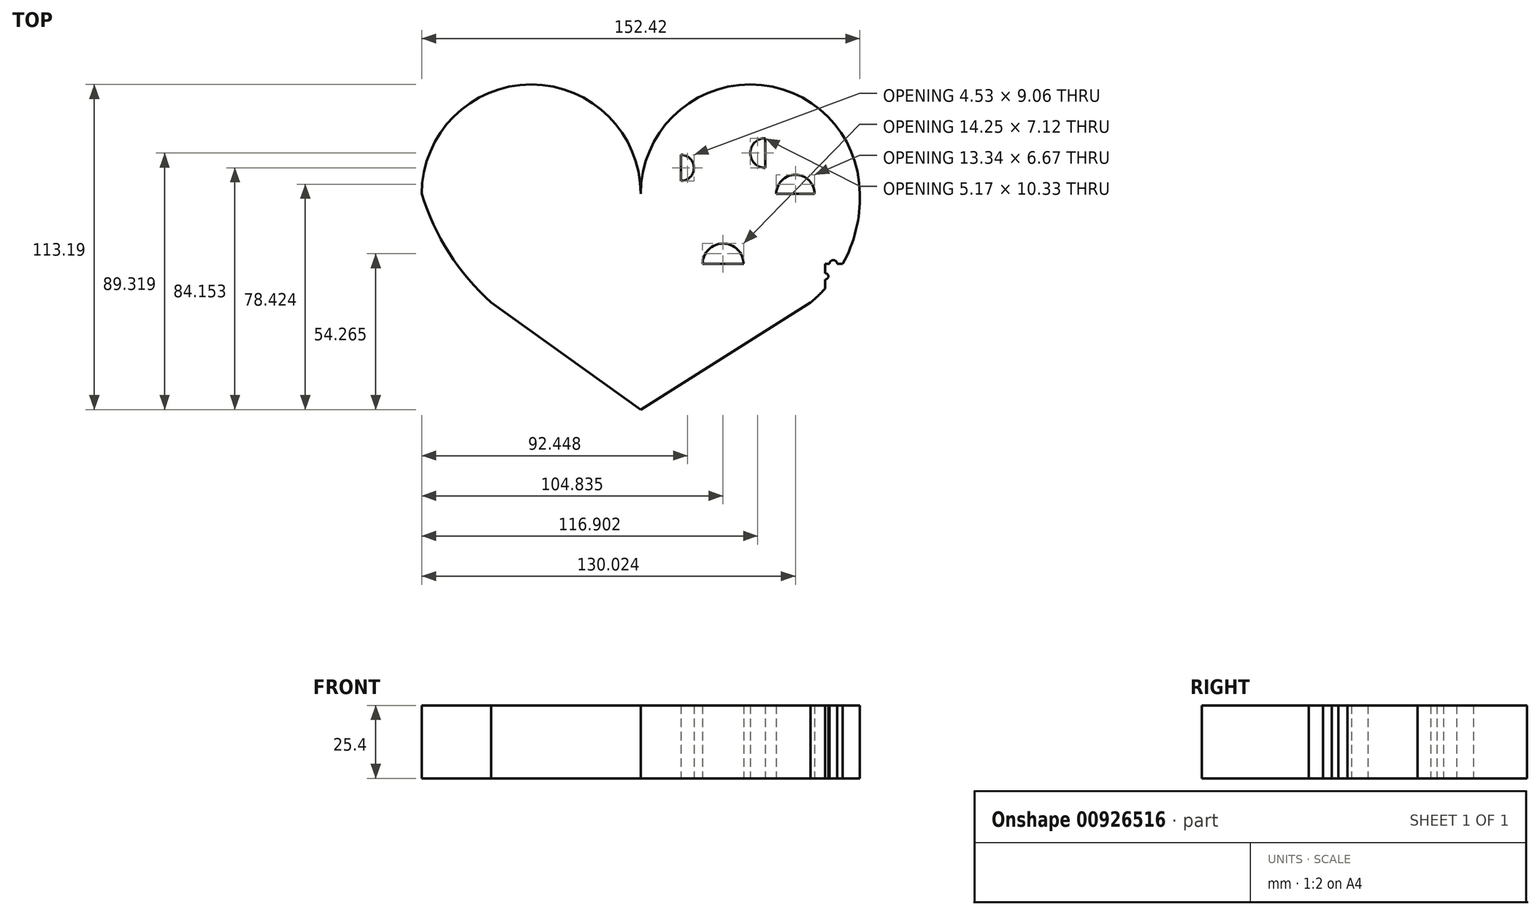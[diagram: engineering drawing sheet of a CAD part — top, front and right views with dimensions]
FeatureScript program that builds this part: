
annotation { "Feature Type Name" : "Feature", "Feature Type Description" : "" }
export const myFeature = defineFeature(function(context is Context, id is Id, definition is map)
    precondition{}
    {
        {
            var Q0;
            Q0=qCreatedBy(makeId("Top.planeOp"),FACE);
            var sketch = newSketch(context, id + "F0", { "sketchPlane" : qUnion([Q0])});
            skLineSegment(sketch, "E0", {"start": v(0, 0) * mm, "end": v(76.2, 0) * mm});
            skArc(sketch, "E1", {"start": v(76.2, 0) * mm, "mid": v(38.1, 38.1) * mm, "end": v(0, 0) * mm});
            skLineSegment(sketch, "E2", {"start": v(0, 0) * mm, "end": v(-76.2, 0) * mm});
            skArc(sketch, "E3", {"start": v(0, 0) * mm, "mid": v(-38.1, 38.1) * mm, "end": v(-76.2, 0) * mm});
            skArc(sketch, "E4", {"start": v(-76.2, 0) * mm, "mid": v(-66.69, -20.55) * mm, "end": v(-52.03, -37.8) * mm});
            skArc(sketch, "E5", {"start": v(59.1, -37.8) * mm, "mid": v(72.02, -20.88) * mm, "end": v(76.2, 0) * mm});
            skLineSegment(sketch, "E6", {"start": v(-52.03, -37.8) * mm, "end": v(0, -75.09) * mm});
            skLineSegment(sketch, "E7", {"start": v(0, -75.09) * mm, "end": v(59.1, -37.8) * mm});
            skLineSegment(sketch, "E8", {"start": v(-38.1, 38.1) * mm, "end": v(-38.1, -47.78) * mm});
            skLineSegment(sketch, "E9", {"start": v(-64.08, 27.87) * mm, "end": v(-64.08, -24.39) * mm});
            skLineSegment(sketch, "E10", {"start": v(-12.26, 28) * mm, "end": v(-12.26, -66.3) * mm});
            skLineSegment(sketch, "E11", {"start": v(13.98, 29.5) * mm, "end": v(13.98, -66.27) * mm});
            skLineSegment(sketch, "E12", {"start": v(64.16, 27.8) * mm, "end": v(64.16, -32.94) * mm});
            skLineSegment(sketch, "E13", {"start": v(-69.99, 20.85) * mm, "end": v(-6.21, 20.85) * mm});
            skLineSegment(sketch, "E14.bottom", {"start": v(6.21, 20.85) * mm, "end": v(69.99, 20.85) * mm});
            skLineSegment(sketch, "E14.top", {"start": v(6.21, 20.85) * mm, "end": v(69.99, 20.85) * mm});
            skLineSegment(sketch, "E14.left", {"start": v(6.21, 20.85) * mm, "end": v(6.21, 20.85) * mm});
            skLineSegment(sketch, "E14.right", {"start": v(69.99, 20.85) * mm, "end": v(69.99, 20.85) * mm});
            skLineSegment(sketch, "E15", {"start": v(-76.2, 0) * mm, "end": v(76.2, 0) * mm});
            skLineSegment(sketch, "E16", {"start": v(-64.08, -24.39) * mm, "end": v(70.25, -24.39) * mm});
            skLineSegment(sketch, "E17", {"start": v(-38.1, -47.78) * mm, "end": v(43.29, -47.78) * mm});
            skLineSegment(sketch, "E18", {"start": v(43.29, -47.78) * mm, "end": v(43.29, 37.75) * mm});
            skArc(sketch, "E19", {"start": v(-65.57, 20.85) * mm, "mid": v(-66.94, 22.19) * mm, "end": v(-68.32, 20.85) * mm});
            skArc(sketch, "E20", {"start": v(-64.08, 25.31) * mm, "mid": v(-65.33, 24.01) * mm, "end": v(-64.08, 22.71) * mm});
            skArc(sketch, "E21", {"start": v(-44.59, 20.85) * mm, "mid": v(-50, 25.72) * mm, "end": v(-55.4, 20.85) * mm});
            skArc(sketch, "E22", {"start": v(-38.1, 33.7) * mm, "mid": v(-43, 29.5) * mm, "end": v(-38.1, 25.31) * mm});
            skArc(sketch, "E23", {"start": v(-32.25, 20.85) * mm, "mid": v(-24.93, 15.14) * mm, "end": v(-17.62, 20.85) * mm});
            skArc(sketch, "E24", {"start": v(-12.26, 25.31) * mm, "mid": v(-15.3, 24.01) * mm, "end": v(-12.26, 22.71) * mm});
            skArc(sketch, "E25", {"start": v(-10.69, 20.85) * mm, "mid": v(-9.65, 18.8) * mm, "end": v(-8.62, 20.85) * mm});
            skArc(sketch, "E26", {"start": v(-64.08, 14.25) * mm, "mid": v(-68.2, 9.75) * mm, "end": v(-64.08, 5.25) * mm});
            skArc(sketch, "E27", {"start": v(-72.46, 0) * mm, "mid": v(-69.6, -2.41) * mm, "end": v(-66.75, 0) * mm});
            skArc(sketch, "E28", {"start": v(-46.12, 0) * mm, "mid": v(-50.71, 4.13) * mm, "end": v(-55.3, 0) * mm});
            skArc(sketch, "E29", {"start": v(-38.1, 4.4) * mm, "mid": v(-33.7, 9.23) * mm, "end": v(-38.1, 14.06) * mm});
            skArc(sketch, "E30", {"start": v(-64.08, -6.97) * mm, "mid": v(-67.6, -12.07) * mm, "end": v(-64.08, -17.17) * mm});
            skArc(sketch, "E31", {"start": v(-45.1, -24.39) * mm, "mid": v(-50.74, -16.9) * mm, "end": v(-56.38, -24.39) * mm});
            skArc(sketch, "E32", {"start": v(-38.1, -20) * mm, "mid": v(-32.5, -13.15) * mm, "end": v(-38.1, -6.3) * mm});
            skArc(sketch, "E33", {"start": v(-30.77, 0) * mm, "mid": v(-24.93, -6.3) * mm, "end": v(-19.1, 0) * mm});
            skArc(sketch, "E34", {"start": v(-12.26, 6.63) * mm, "mid": v(-6.96, 10.1) * mm, "end": v(-12.26, 13.57) * mm});
            skArc(sketch, "E35", {"start": v(-12.26, -17.17) * mm, "mid": v(-8.44, -13.07) * mm, "end": v(-12.26, -8.97) * mm});
            skArc(sketch, "E36", {"start": v(-38.1, -31) * mm, "mid": v(-43.58, -35.9) * mm, "end": v(-38.1, -40.81) * mm});
            skArc(sketch, "E37", {"start": v(-27.8, -24.39) * mm, "mid": v(-24.06, -29.29) * mm, "end": v(-20.3, -24.39) * mm});
            skArc(sketch, "E38", {"start": v(-18.77, -47.78) * mm, "mid": v(-24.34, -38.75) * mm, "end": v(-29.92, -47.78) * mm});
            skArc(sketch, "E39", {"start": v(-12.26, -41) * mm, "mid": v(-6.98, -36.58) * mm, "end": v(-12.26, -32.16) * mm});
            skArc(sketch, "E40", {"start": v(-12.26, -52.9) * mm, "mid": v(-16.92, -57.22) * mm, "end": v(-12.26, -61.53) * mm});
            skArc(sketch, "E41", {"start": v(-3.1, 0) * mm, "mid": v(2.14, -6.27) * mm, "end": v(7.37, 0) * mm});
            skArc(sketch, "E42", {"start": v(13.98, -18.39) * mm, "mid": v(20.73, -13.9) * mm, "end": v(13.98, -9.4) * mm});
            skArc(sketch, "E43", {"start": v(-7.2, -24.39) * mm, "mid": v(-0.12, -31.84) * mm, "end": v(6.96, -24.39) * mm});
            skArc(sketch, "E44", {"start": v(13.98, -31.77) * mm, "mid": v(4.35, -36.7) * mm, "end": v(13.98, -41.62) * mm});
            skArc(sketch, "E45", {"start": v(-6.17, -47.78) * mm, "mid": v(-0.32, -55.88) * mm, "end": v(5.53, -47.78) * mm});
            skArc(sketch, "E46", {"start": v(13.98, -54.96) * mm, "mid": v(8.36, -57.83) * mm, "end": v(13.98, -60.7) * mm});
            skArc(sketch, "E47", {"start": v(20.54, 0) * mm, "mid": v(25.92, 5.38) * mm, "end": v(31.3, 0) * mm});
            skArc(sketch, "E48", {"start": v(13.98, 13.6) * mm, "mid": v(18.51, 9.06) * mm, "end": v(13.98, 4.53) * mm});
            skArc(sketch, "E49", {"start": v(7.98, 20.85) * mm, "mid": v(10.72, 23.6) * mm, "end": v(13.46, 20.85) * mm});
            skArc(sketch, "E50", {"start": v(13.98, 28.16) * mm, "mid": v(11.84, 26.02) * mm, "end": v(13.98, 23.87) * mm});
            skArc(sketch, "E51", {"start": v(22.74, 19.59) * mm, "mid": v(28.3, 27.14) * mm, "end": v(35.26, 20.85) * mm});
            skArc(sketch, "E52", {"start": v(43.29, 33.52) * mm, "mid": v(39, 29.23) * mm, "end": v(43.29, 24.95) * mm});
            skArc(sketch, "E53", {"start": v(43.29, 9.06) * mm, "mid": v(38.12, 14.23) * mm, "end": v(43.29, 19.4) * mm});
            skArc(sketch, "E54", {"start": v(48.58, 20.85) * mm, "mid": v(54.42, 15.02) * mm, "end": v(60.25, 20.85) * mm});
            skArc(sketch, "E55", {"start": v(64.16, 25.9) * mm, "mid": v(61.59, 23.78) * mm, "end": v(63.17, 20.85) * mm});
            skArc(sketch, "E56", {"start": v(68.7, 20.85) * mm, "mid": v(67.28, 19.42) * mm, "end": v(65.85, 20.85) * mm});
            skArc(sketch, "E57", {"start": v(64.16, 15.78) * mm, "mid": v(58.44, 10.06) * mm, "end": v(64.16, 4.35) * mm});
            skArc(sketch, "E58", {"start": v(47.16, 0) * mm, "mid": v(53.82, 6.67) * mm, "end": v(60.5, 0) * mm});
            skArc(sketch, "E59", {"start": v(21.51, -24.39) * mm, "mid": v(28.63, -17.26) * mm, "end": v(35.76, -24.39) * mm});
            skArc(sketch, "E60", {"start": v(43.29, -5.02) * mm, "mid": v(35.18, -13.13) * mm, "end": v(43.29, -21.24) * mm});
            skArc(sketch, "E61", {"start": v(48.88, -24.39) * mm, "mid": v(56.38, -31.89) * mm, "end": v(63.88, -24.39) * mm});
            skArc(sketch, "E62", {"start": v(64.16, -7.88) * mm, "mid": v(69.03, -12.75) * mm, "end": v(64.16, -17.63) * mm});
            skArc(sketch, "E63", {"start": v(21.14, -47.78) * mm, "mid": v(28.26, -40.66) * mm, "end": v(35.38, -47.78) * mm});
            skArc(sketch, "E64", {"start": v(43.29, -29.25) * mm, "mid": v(35.84, -36.7) * mm, "end": v(43.29, -44.13) * mm});
            skArc(sketch, "E65", {"start": v(64.16, -27.59) * mm, "mid": v(65.26, -28.69) * mm, "end": v(64.16, -29.8) * mm});
            skArc(sketch, "E66", {"start": v(65.65, -24.39) * mm, "mid": v(67, -23.05) * mm, "end": v(68.33, -24.39) * mm});
            skSolve(sketch);
        }
        {
            var Q0;
            {var subQ3=sQuery(id+"F0.wireOp",EDGE,"E41");Q0=makeQuery(id+"F0.imprint","IMPRINT",FACE,{"disambiguationData":[TD([[makeQuery(id+"F0.imprint","IMPRINT",EDGE,{"derivedFrom":subQ3}),1.0]])]});}
            var Q1;
            {var subQ1=sQuery(id+"F0.wireOp",EDGE,"E14.bottom");var subQ6=sQuery(id+"F0.wireOp",EDGE,"E1");var subQ9=makeQuery(id+"F0.imprint","INTERSECT",VERTEX,{"disambiguationData":[OD(0.0)],"derivedFrom":[subQ6,subQ1]});Q1=makeQuery(id+"F0.imprint","IMPRINT",FACE,{"disambiguationData":[TD([[makeQuery(id+"F0.imprint","IMPRINT",EDGE,{"disambiguationData":[TD([[subQ9,-1.0]])],"derivedFrom":subQ6}),1.0]])]});}
            var Q2;
            {var subQ0=sQuery(id+"F0.wireOp",EDGE,"E49");Q2=makeQuery(id+"F0.imprint","IMPRINT",FACE,{"disambiguationData":[TD([[makeQuery(id+"F0.imprint","IMPRINT",EDGE,{"derivedFrom":subQ0}),1.0]])]});}
            var Q3;
            {var subQ0=sQuery(id+"F0.wireOp",EDGE,"E13");var subQ6=sQuery(id+"F0.wireOp",EDGE,"E3");var subQ8=makeQuery(id+"F0.imprint","INTERSECT",VERTEX,{"disambiguationData":[OD(0.0)],"derivedFrom":[subQ6,subQ0]});Q3=makeQuery(id+"F0.imprint","IMPRINT",FACE,{"disambiguationData":[TD([[makeQuery(id+"F0.imprint","IMPRINT",EDGE,{"disambiguationData":[TD([[subQ8,-1.0]])],"derivedFrom":subQ6}),1.0]])]});}
            var Q4;
            {var subQ0=sQuery(id+"F0.wireOp",EDGE,"E19");Q4=makeQuery(id+"F0.imprint","IMPRINT",FACE,{"disambiguationData":[TD([[makeQuery(id+"F0.imprint","IMPRINT",EDGE,{"derivedFrom":subQ0}),-1.0]])]});}
            var Q5;
            {var subQ6=sQuery(id+"F0.wireOp",EDGE,"E27");Q5=makeQuery(id+"F0.imprint","IMPRINT",FACE,{"disambiguationData":[TD([[makeQuery(id+"F0.imprint","IMPRINT",EDGE,{"derivedFrom":subQ6}),-1.0]])]});}
            var Q6;
            {var subQ3=sQuery(id+"F0.wireOp",EDGE,"E36");Q6=makeQuery(id+"F0.imprint","IMPRINT",FACE,{"disambiguationData":[TD([[makeQuery(id+"F0.imprint","IMPRINT",EDGE,{"derivedFrom":subQ3}),-1.0]])]});}
            var Q7;
            {var subQ4=sQuery(id+"F0.wireOp",EDGE,"E65");Q7=makeQuery(id+"F0.imprint","IMPRINT",FACE,{"disambiguationData":[TD([[makeQuery(id+"F0.imprint","IMPRINT",EDGE,{"derivedFrom":subQ4}),1.0]])]});}
            var Q8;
            {var subQ4=sQuery(id+"F0.wireOp",EDGE,"E40");Q8=makeQuery(id+"F0.imprint","IMPRINT",FACE,{"disambiguationData":[TD([[makeQuery(id+"F0.imprint","IMPRINT",EDGE,{"derivedFrom":subQ4}),-1.0]])]});}
            var Q9;
            {var subQ0=sQuery(id+"F0.wireOp",EDGE,"E11");var subQ3=sQuery(id+"F0.wireOp",EDGE,"E46");var subQ5=makeQuery(id+"F0.imprint","INTERSECT",VERTEX,{"disambiguationData":[OD(0.0)],"derivedFrom":[subQ0,subQ3]});Q9=makeQuery(id+"F0.imprint","IMPRINT",FACE,{"disambiguationData":[TD([[makeQuery(id+"F0.imprint","IMPRINT",EDGE,{"disambiguationData":[TD([[subQ5,1.0]])],"derivedFrom":subQ0}),1.0]])]});}
            var Q10;
            {var subQ6=sQuery(id+"F0.wireOp",EDGE,"E56");Q10=makeQuery(id+"F0.imprint","IMPRINT",FACE,{"disambiguationData":[TD([[makeQuery(id+"F0.imprint","IMPRINT",EDGE,{"derivedFrom":subQ6}),1.0]])]});}
            var Q11;
            {var subQ3=sQuery(id+"F0.wireOp",EDGE,"E62");Q11=makeQuery(id+"F0.imprint","IMPRINT",FACE,{"disambiguationData":[TD([[makeQuery(id+"F0.imprint","IMPRINT",EDGE,{"derivedFrom":subQ3}),1.0]])]});}
            var Q12;
            {var subQ6=sQuery(id+"F0.wireOp",EDGE,"E55");Q12=makeQuery(id+"F0.imprint","IMPRINT",FACE,{"disambiguationData":[TD([[makeQuery(id+"F0.imprint","IMPRINT",EDGE,{"derivedFrom":subQ6}),-1.0]])]});}
            var Q13;
            {var subQ11=sQuery(id+"F0.wireOp",EDGE,"E52");Q13=makeQuery(id+"F0.imprint","IMPRINT",FACE,{"disambiguationData":[TD([[makeQuery(id+"F0.imprint","IMPRINT",EDGE,{"derivedFrom":subQ11}),-1.0]])]});}
            var Q14;
            {var subQ5=sQuery(id+"F0.wireOp",EDGE,"E0");var subQ7=makeQuery(id+"F0.imprint","INTERSECT",VERTEX,{"derivedFrom":[subQ5,sQuery(id+"F0.wireOp",EDGE,"E41")]});Q14=makeQuery(id+"F0.imprint","IMPRINT",FACE,{"disambiguationData":[TD([[makeQuery(id+"F0.imprint","IMPRINT",EDGE,{"disambiguationData":[TD([[subQ7,-1.0]])],"derivedFrom":subQ5}),1.0]])]});}
            var Q15;
            {var subQ9=sQuery(id+"F0.wireOp",EDGE,"E25");Q15=makeQuery(id+"F0.imprint","IMPRINT",FACE,{"disambiguationData":[TD([[makeQuery(id+"F0.imprint","IMPRINT",EDGE,{"derivedFrom":subQ9}),-1.0]])]});}
            var Q16;
            {var subQ8=sQuery(id+"F0.wireOp",EDGE,"E24");Q16=makeQuery(id+"F0.imprint","IMPRINT",FACE,{"disambiguationData":[TD([[makeQuery(id+"F0.imprint","IMPRINT",EDGE,{"derivedFrom":subQ8}),-1.0]])]});}
            var Q17;
            {var subQ4=sQuery(id+"F0.wireOp",EDGE,"E21");Q17=makeQuery(id+"F0.imprint","IMPRINT",FACE,{"disambiguationData":[TD([[makeQuery(id+"F0.imprint","IMPRINT",EDGE,{"derivedFrom":subQ4}),-1.0]])]});}
            var Q18;
            {var subQ13=sQuery(id+"F0.wireOp",EDGE,"E26");Q18=makeQuery(id+"F0.imprint","IMPRINT",FACE,{"disambiguationData":[TD([[makeQuery(id+"F0.imprint","IMPRINT",EDGE,{"derivedFrom":subQ13}),-1.0]])]});}
            var Q19;
            {var subQ5=sQuery(id+"F0.wireOp",EDGE,"E61");Q19=makeQuery(id+"F0.imprint","IMPRINT",FACE,{"disambiguationData":[TD([[makeQuery(id+"F0.imprint","IMPRINT",EDGE,{"derivedFrom":subQ5}),-1.0]])]});}
            var Q20;
            {var subQ0=sQuery(id+"F0.wireOp",EDGE,"E45");Q20=makeQuery(id+"F0.imprint","IMPRINT",FACE,{"disambiguationData":[TD([[makeQuery(id+"F0.imprint","IMPRINT",EDGE,{"derivedFrom":subQ0}),-1.0]])]});}
            var Q21;
            {var subQ0=sQuery(id+"F0.wireOp",EDGE,"E31");Q21=makeQuery(id+"F0.imprint","IMPRINT",FACE,{"disambiguationData":[TD([[makeQuery(id+"F0.imprint","IMPRINT",EDGE,{"derivedFrom":subQ0}),-1.0]])]});}
            var Q22;
            {var subQ12=sQuery(id+"F0.wireOp",EDGE,"E37");Q22=makeQuery(id+"F0.imprint","IMPRINT",FACE,{"disambiguationData":[TD([[makeQuery(id+"F0.imprint","IMPRINT",EDGE,{"derivedFrom":subQ12}),-1.0]])]});}
            var Q23;
            {var subQ4=sQuery(id+"F0.wireOp",EDGE,"E63");Q23=makeQuery(id+"F0.imprint","IMPRINT",FACE,{"disambiguationData":[TD([[makeQuery(id+"F0.imprint","IMPRINT",EDGE,{"derivedFrom":subQ4}),1.0]])]});}
            var Q24;
            {var subQ15=sQuery(id+"F0.wireOp",EDGE,"E35");Q24=makeQuery(id+"F0.imprint","IMPRINT",FACE,{"disambiguationData":[TD([[makeQuery(id+"F0.imprint","IMPRINT",EDGE,{"derivedFrom":subQ15}),-1.0]])]});}
            var Q25;
            {var subQ15=sQuery(id+"F0.wireOp",EDGE,"E32");Q25=makeQuery(id+"F0.imprint","IMPRINT",FACE,{"disambiguationData":[TD([[makeQuery(id+"F0.imprint","IMPRINT",EDGE,{"derivedFrom":subQ15}),-1.0]])]});}
            var Q26;
            {var subQ4=sQuery(id+"F0.wireOp",EDGE,"E42");Q26=makeQuery(id+"F0.imprint","IMPRINT",FACE,{"disambiguationData":[TD([[makeQuery(id+"F0.imprint","IMPRINT",EDGE,{"derivedFrom":subQ4}),-1.0]])]});}
            var Q27;
            {var subQ11=sQuery(id+"F0.wireOp",EDGE,"E0");var subQ16=sQuery(id+"F0.wireOp",EDGE,"E58");var subQ17=makeQuery(id+"F0.imprint","INTERSECT",VERTEX,{"disambiguationData":[OD(0.0)],"derivedFrom":[subQ11,subQ16]});Q27=makeQuery(id+"F0.imprint","IMPRINT",FACE,{"disambiguationData":[TD([[makeQuery(id+"F0.imprint","IMPRINT",EDGE,{"disambiguationData":[TD([[subQ17,-1.0]])],"derivedFrom":subQ11}),-1.0]])]});}
            var Q28;
            {var subQ4=sQuery(id+"F0.wireOp",EDGE,"E47");Q28=makeQuery(id+"F0.imprint","IMPRINT",FACE,{"disambiguationData":[TD([[makeQuery(id+"F0.imprint","IMPRINT",EDGE,{"derivedFrom":subQ4}),1.0]])]});}
            var Q29;
            {var subQ8=sQuery(id+"F0.wireOp",EDGE,"E54");Q29=makeQuery(id+"F0.imprint","IMPRINT",FACE,{"disambiguationData":[TD([[makeQuery(id+"F0.imprint","IMPRINT",EDGE,{"derivedFrom":subQ8}),-1.0]])]});}
            var Q30;
            {var subQ3=sQuery(id+"F0.wireOp",EDGE,"E23");Q30=makeQuery(id+"F0.imprint","IMPRINT",FACE,{"disambiguationData":[TD([[makeQuery(id+"F0.imprint","IMPRINT",EDGE,{"derivedFrom":subQ3}),-1.0]])]});}
            var Q31;
            {var subQ9=sQuery(id+"F0.wireOp",EDGE,"E28");Q31=makeQuery(id+"F0.imprint","IMPRINT",FACE,{"disambiguationData":[TD([[makeQuery(id+"F0.imprint","IMPRINT",EDGE,{"derivedFrom":subQ9}),-1.0]])]});}
            var Q32;
            {var subQ4=sQuery(id+"F0.wireOp",EDGE,"E39");Q32=makeQuery(id+"F0.imprint","IMPRINT",FACE,{"disambiguationData":[TD([[makeQuery(id+"F0.imprint","IMPRINT",EDGE,{"derivedFrom":subQ4}),-1.0]])]});}
            var Q33;
            {var subQ0=sQuery(id+"F0.wireOp",EDGE,"E25");Q33=makeQuery(id+"F0.imprint","IMPRINT",FACE,{"disambiguationData":[TD([[makeQuery(id+"F0.imprint","IMPRINT",EDGE,{"derivedFrom":subQ0}),1.0]])]});}
            var Q34;
            {var subQ0=sQuery(id+"F0.wireOp",EDGE,"E24");Q34=makeQuery(id+"F0.imprint","IMPRINT",FACE,{"disambiguationData":[TD([[makeQuery(id+"F0.imprint","IMPRINT",EDGE,{"derivedFrom":subQ0}),1.0]])]});}
            var Q35;
            {var subQ0=sQuery(id+"F0.wireOp",EDGE,"E23");Q35=makeQuery(id+"F0.imprint","IMPRINT",FACE,{"disambiguationData":[TD([[makeQuery(id+"F0.imprint","IMPRINT",EDGE,{"derivedFrom":subQ0}),1.0]])]});}
            var Q36;
            {var subQ0=sQuery(id+"F0.wireOp",EDGE,"E34");Q36=makeQuery(id+"F0.imprint","IMPRINT",FACE,{"disambiguationData":[TD([[makeQuery(id+"F0.imprint","IMPRINT",EDGE,{"derivedFrom":subQ0}),1.0]])]});}
            var Q37;
            {var subQ0=sQuery(id+"F0.wireOp",EDGE,"E33");Q37=makeQuery(id+"F0.imprint","IMPRINT",FACE,{"disambiguationData":[TD([[makeQuery(id+"F0.imprint","IMPRINT",EDGE,{"derivedFrom":subQ0}),1.0]])]});}
            var Q38;
            {var subQ0=sQuery(id+"F0.wireOp",EDGE,"E29");Q38=makeQuery(id+"F0.imprint","IMPRINT",FACE,{"disambiguationData":[TD([[makeQuery(id+"F0.imprint","IMPRINT",EDGE,{"derivedFrom":subQ0}),1.0]])]});}
            var Q39;
            {var subQ0=sQuery(id+"F0.wireOp",EDGE,"E22");Q39=makeQuery(id+"F0.imprint","IMPRINT",FACE,{"disambiguationData":[TD([[makeQuery(id+"F0.imprint","IMPRINT",EDGE,{"derivedFrom":subQ0}),1.0]])]});}
            var Q40;
            {var subQ0=sQuery(id+"F0.wireOp",EDGE,"E21");Q40=makeQuery(id+"F0.imprint","IMPRINT",FACE,{"disambiguationData":[TD([[makeQuery(id+"F0.imprint","IMPRINT",EDGE,{"derivedFrom":subQ0}),1.0]])]});}
            var Q41;
            {var subQ0=sQuery(id+"F0.wireOp",EDGE,"E20");Q41=makeQuery(id+"F0.imprint","IMPRINT",FACE,{"disambiguationData":[TD([[makeQuery(id+"F0.imprint","IMPRINT",EDGE,{"derivedFrom":subQ0}),1.0]])]});}
            var Q42;
            {var subQ0=sQuery(id+"F0.wireOp",EDGE,"E19");Q42=makeQuery(id+"F0.imprint","IMPRINT",FACE,{"disambiguationData":[TD([[makeQuery(id+"F0.imprint","IMPRINT",EDGE,{"derivedFrom":subQ0}),1.0]])]});}
            var Q43;
            {var subQ0=sQuery(id+"F0.wireOp",EDGE,"E26");Q43=makeQuery(id+"F0.imprint","IMPRINT",FACE,{"disambiguationData":[TD([[makeQuery(id+"F0.imprint","IMPRINT",EDGE,{"derivedFrom":subQ0}),1.0]])]});}
            var Q44;
            {var subQ0=sQuery(id+"F0.wireOp",EDGE,"E27");Q44=makeQuery(id+"F0.imprint","IMPRINT",FACE,{"disambiguationData":[TD([[makeQuery(id+"F0.imprint","IMPRINT",EDGE,{"derivedFrom":subQ0}),1.0]])]});}
            var Q45;
            {var subQ0=sQuery(id+"F0.wireOp",EDGE,"E30");Q45=makeQuery(id+"F0.imprint","IMPRINT",FACE,{"disambiguationData":[TD([[makeQuery(id+"F0.imprint","IMPRINT",EDGE,{"derivedFrom":subQ0}),1.0]])]});}
            var Q46;
            {var subQ0=sQuery(id+"F0.wireOp",EDGE,"E31");Q46=makeQuery(id+"F0.imprint","IMPRINT",FACE,{"disambiguationData":[TD([[makeQuery(id+"F0.imprint","IMPRINT",EDGE,{"derivedFrom":subQ0}),1.0]])]});}
            var Q47;
            {var subQ0=sQuery(id+"F0.wireOp",EDGE,"E32");Q47=makeQuery(id+"F0.imprint","IMPRINT",FACE,{"disambiguationData":[TD([[makeQuery(id+"F0.imprint","IMPRINT",EDGE,{"derivedFrom":subQ0}),1.0]])]});}
            var Q48;
            {var subQ0=sQuery(id+"F0.wireOp",EDGE,"E28");Q48=makeQuery(id+"F0.imprint","IMPRINT",FACE,{"disambiguationData":[TD([[makeQuery(id+"F0.imprint","IMPRINT",EDGE,{"derivedFrom":subQ0}),1.0]])]});}
            var Q49;
            {var subQ0=sQuery(id+"F0.wireOp",EDGE,"E35");Q49=makeQuery(id+"F0.imprint","IMPRINT",FACE,{"disambiguationData":[TD([[makeQuery(id+"F0.imprint","IMPRINT",EDGE,{"derivedFrom":subQ0}),1.0]])]});}
            var Q50;
            {var subQ0=sQuery(id+"F0.wireOp",EDGE,"E37");Q50=makeQuery(id+"F0.imprint","IMPRINT",FACE,{"disambiguationData":[TD([[makeQuery(id+"F0.imprint","IMPRINT",EDGE,{"derivedFrom":subQ0}),1.0]])]});}
            var Q51;
            {var subQ0=sQuery(id+"F0.wireOp",EDGE,"E36");Q51=makeQuery(id+"F0.imprint","IMPRINT",FACE,{"disambiguationData":[TD([[makeQuery(id+"F0.imprint","IMPRINT",EDGE,{"derivedFrom":subQ0}),1.0]])]});}
            var Q52;
            {var subQ0=sQuery(id+"F0.wireOp",EDGE,"E38");Q52=makeQuery(id+"F0.imprint","IMPRINT",FACE,{"disambiguationData":[TD([[makeQuery(id+"F0.imprint","IMPRINT",EDGE,{"derivedFrom":subQ0}),1.0]])]});}
            var Q53;
            {var subQ0=sQuery(id+"F0.wireOp",EDGE,"E39");Q53=makeQuery(id+"F0.imprint","IMPRINT",FACE,{"disambiguationData":[TD([[makeQuery(id+"F0.imprint","IMPRINT",EDGE,{"derivedFrom":subQ0}),1.0]])]});}
            var Q54;
            {var subQ0=sQuery(id+"F0.wireOp",EDGE,"E43");Q54=makeQuery(id+"F0.imprint","IMPRINT",FACE,{"disambiguationData":[TD([[makeQuery(id+"F0.imprint","IMPRINT",EDGE,{"derivedFrom":subQ0}),1.0]])]});}
            var Q55;
            {var subQ0=sQuery(id+"F0.wireOp",EDGE,"E44");Q55=makeQuery(id+"F0.imprint","IMPRINT",FACE,{"disambiguationData":[TD([[makeQuery(id+"F0.imprint","IMPRINT",EDGE,{"derivedFrom":subQ0}),1.0]])]});}
            var Q56;
            {var subQ0=sQuery(id+"F0.wireOp",EDGE,"E45");Q56=makeQuery(id+"F0.imprint","IMPRINT",FACE,{"disambiguationData":[TD([[makeQuery(id+"F0.imprint","IMPRINT",EDGE,{"derivedFrom":subQ0}),1.0]])]});}
            var Q57;
            {var subQ0=sQuery(id+"F0.wireOp",EDGE,"E46");Q57=makeQuery(id+"F0.imprint","IMPRINT",FACE,{"disambiguationData":[TD([[makeQuery(id+"F0.imprint","IMPRINT",EDGE,{"derivedFrom":subQ0}),1.0]])]});}
            var Q58;
            {var subQ0=sQuery(id+"F0.wireOp",EDGE,"E40");Q58=makeQuery(id+"F0.imprint","IMPRINT",FACE,{"disambiguationData":[TD([[makeQuery(id+"F0.imprint","IMPRINT",EDGE,{"derivedFrom":subQ0}),1.0]])]});}
            var Q59;
            {var subQ0=sQuery(id+"F0.wireOp",EDGE,"E63");Q59=makeQuery(id+"F0.imprint","IMPRINT",FACE,{"disambiguationData":[TD([[makeQuery(id+"F0.imprint","IMPRINT",EDGE,{"derivedFrom":subQ0}),-1.0]])]});}
            var Q60;
            {var subQ0=sQuery(id+"F0.wireOp",EDGE,"E64");Q60=makeQuery(id+"F0.imprint","IMPRINT",FACE,{"disambiguationData":[TD([[makeQuery(id+"F0.imprint","IMPRINT",EDGE,{"derivedFrom":subQ0}),1.0]])]});}
            var Q61;
            {var subQ0=sQuery(id+"F0.wireOp",EDGE,"E59");Q61=makeQuery(id+"F0.imprint","IMPRINT",FACE,{"disambiguationData":[TD([[makeQuery(id+"F0.imprint","IMPRINT",EDGE,{"derivedFrom":subQ0}),-1.0]])]});}
            var Q62;
            {var subQ0=sQuery(id+"F0.wireOp",EDGE,"E62");Q62=makeQuery(id+"F0.imprint","IMPRINT",FACE,{"disambiguationData":[TD([[makeQuery(id+"F0.imprint","IMPRINT",EDGE,{"derivedFrom":subQ0}),-1.0]])]});}
            var Q63;
            {var subQ0=sQuery(id+"F0.wireOp",EDGE,"E60");Q63=makeQuery(id+"F0.imprint","IMPRINT",FACE,{"disambiguationData":[TD([[makeQuery(id+"F0.imprint","IMPRINT",EDGE,{"derivedFrom":subQ0}),1.0]])]});}
            var Q64;
            {var subQ0=sQuery(id+"F0.wireOp",EDGE,"E47");Q64=makeQuery(id+"F0.imprint","IMPRINT",FACE,{"disambiguationData":[TD([[makeQuery(id+"F0.imprint","IMPRINT",EDGE,{"derivedFrom":subQ0}),-1.0]])]});}
            var Q65;
            {var subQ0=sQuery(id+"F0.wireOp",EDGE,"E48");Q65=makeQuery(id+"F0.imprint","IMPRINT",FACE,{"disambiguationData":[TD([[makeQuery(id+"F0.imprint","IMPRINT",EDGE,{"derivedFrom":subQ0}),-1.0]])]});}
            var Q66;
            {var subQ0=sQuery(id+"F0.wireOp",EDGE,"E53");Q66=makeQuery(id+"F0.imprint","IMPRINT",FACE,{"disambiguationData":[TD([[makeQuery(id+"F0.imprint","IMPRINT",EDGE,{"derivedFrom":subQ0}),-1.0]])]});}
            var Q67;
            {var subQ0=sQuery(id+"F0.wireOp",EDGE,"E54");Q67=makeQuery(id+"F0.imprint","IMPRINT",FACE,{"disambiguationData":[TD([[makeQuery(id+"F0.imprint","IMPRINT",EDGE,{"derivedFrom":subQ0}),1.0]])]});}
            var Q68;
            {var subQ0=sQuery(id+"F0.wireOp",EDGE,"E57");Q68=makeQuery(id+"F0.imprint","IMPRINT",FACE,{"disambiguationData":[TD([[makeQuery(id+"F0.imprint","IMPRINT",EDGE,{"derivedFrom":subQ0}),1.0]])]});}
            var Q69;
            {var subQ0=sQuery(id+"F0.wireOp",EDGE,"E58");Q69=makeQuery(id+"F0.imprint","IMPRINT",FACE,{"disambiguationData":[TD([[makeQuery(id+"F0.imprint","IMPRINT",EDGE,{"derivedFrom":subQ0}),-1.0]])]});}
            var Q70;
            {var subQ0=sQuery(id+"F0.wireOp",EDGE,"E42");Q70=makeQuery(id+"F0.imprint","IMPRINT",FACE,{"disambiguationData":[TD([[makeQuery(id+"F0.imprint","IMPRINT",EDGE,{"derivedFrom":subQ0}),1.0]])]});}
            var Q71;
            {var subQ0=sQuery(id+"F0.wireOp",EDGE,"E55");Q71=makeQuery(id+"F0.imprint","IMPRINT",FACE,{"disambiguationData":[TD([[makeQuery(id+"F0.imprint","IMPRINT",EDGE,{"derivedFrom":subQ0}),1.0]])]});}
            var Q72;
            {var subQ0=sQuery(id+"F0.wireOp",EDGE,"E56");Q72=makeQuery(id+"F0.imprint","IMPRINT",FACE,{"disambiguationData":[TD([[makeQuery(id+"F0.imprint","IMPRINT",EDGE,{"derivedFrom":subQ0}),-1.0]])]});}
            var Q73;
            {var subQ0=sQuery(id+"F0.wireOp",EDGE,"E51");var subQ1=sQuery(id+"F0.wireOp",EDGE,"E14.bottom");var subQ2=makeQuery(id+"F0.imprint","INTERSECT",VERTEX,{"disambiguationData":[OD(0.0)],"derivedFrom":[subQ1,subQ0]});Q73=makeQuery(id+"F0.imprint","IMPRINT",FACE,{"disambiguationData":[TD([[makeQuery(id+"F0.imprint","IMPRINT",EDGE,{"disambiguationData":[TD([[subQ2,-1.0]])],"derivedFrom":subQ1}),1.0]])]});}
            var Q74;
            {var subQ0=sQuery(id+"F0.wireOp",EDGE,"E50");Q74=makeQuery(id+"F0.imprint","IMPRINT",FACE,{"disambiguationData":[TD([[makeQuery(id+"F0.imprint","IMPRINT",EDGE,{"derivedFrom":subQ0}),1.0]])]});}
            var Q75;
            {var subQ0=sQuery(id+"F0.wireOp",EDGE,"E49");Q75=makeQuery(id+"F0.imprint","IMPRINT",FACE,{"disambiguationData":[TD([[makeQuery(id+"F0.imprint","IMPRINT",EDGE,{"derivedFrom":subQ0}),-1.0]])]});}
            var Q76;
            {var subQ0=sQuery(id+"F0.wireOp",EDGE,"E52");Q76=makeQuery(id+"F0.imprint","IMPRINT",FACE,{"disambiguationData":[TD([[makeQuery(id+"F0.imprint","IMPRINT",EDGE,{"derivedFrom":subQ0}),1.0]])]});}
            var Q77;
            {var subQ0=sQuery(id+"F0.wireOp",EDGE,"E61");Q77=makeQuery(id+"F0.imprint","IMPRINT",FACE,{"disambiguationData":[TD([[makeQuery(id+"F0.imprint","IMPRINT",EDGE,{"derivedFrom":subQ0}),1.0]])]});}
            extrude(context, id + "F1", {"entities" : qUnion([Q0, Q1, Q2, Q3, Q4, Q5, Q6, Q7, Q8, Q9, Q10, Q11, Q12, Q13, Q14, Q15, Q16, Q17, Q18, Q19, Q20, Q21, Q22, Q23, Q24, Q25, Q26, Q27, Q28, Q29, Q30, Q31, Q32, Q33, Q34, Q35, Q36, Q37, Q38, Q39, Q40, Q41, Q42, Q43, Q44, Q45, Q46, Q47, Q48, Q49, Q50, Q51, Q52, Q53, Q54, Q55, Q56, Q57, Q58, Q59, Q60, Q61, Q62, Q63, Q64, Q65, Q66, Q67, Q68, Q69, Q70, Q71, Q72, Q73, Q74, Q75, Q76, Q77]), "depth" : 25.4 * mm, "offsetDistance" : 25.4 * mm});
        }
    });
